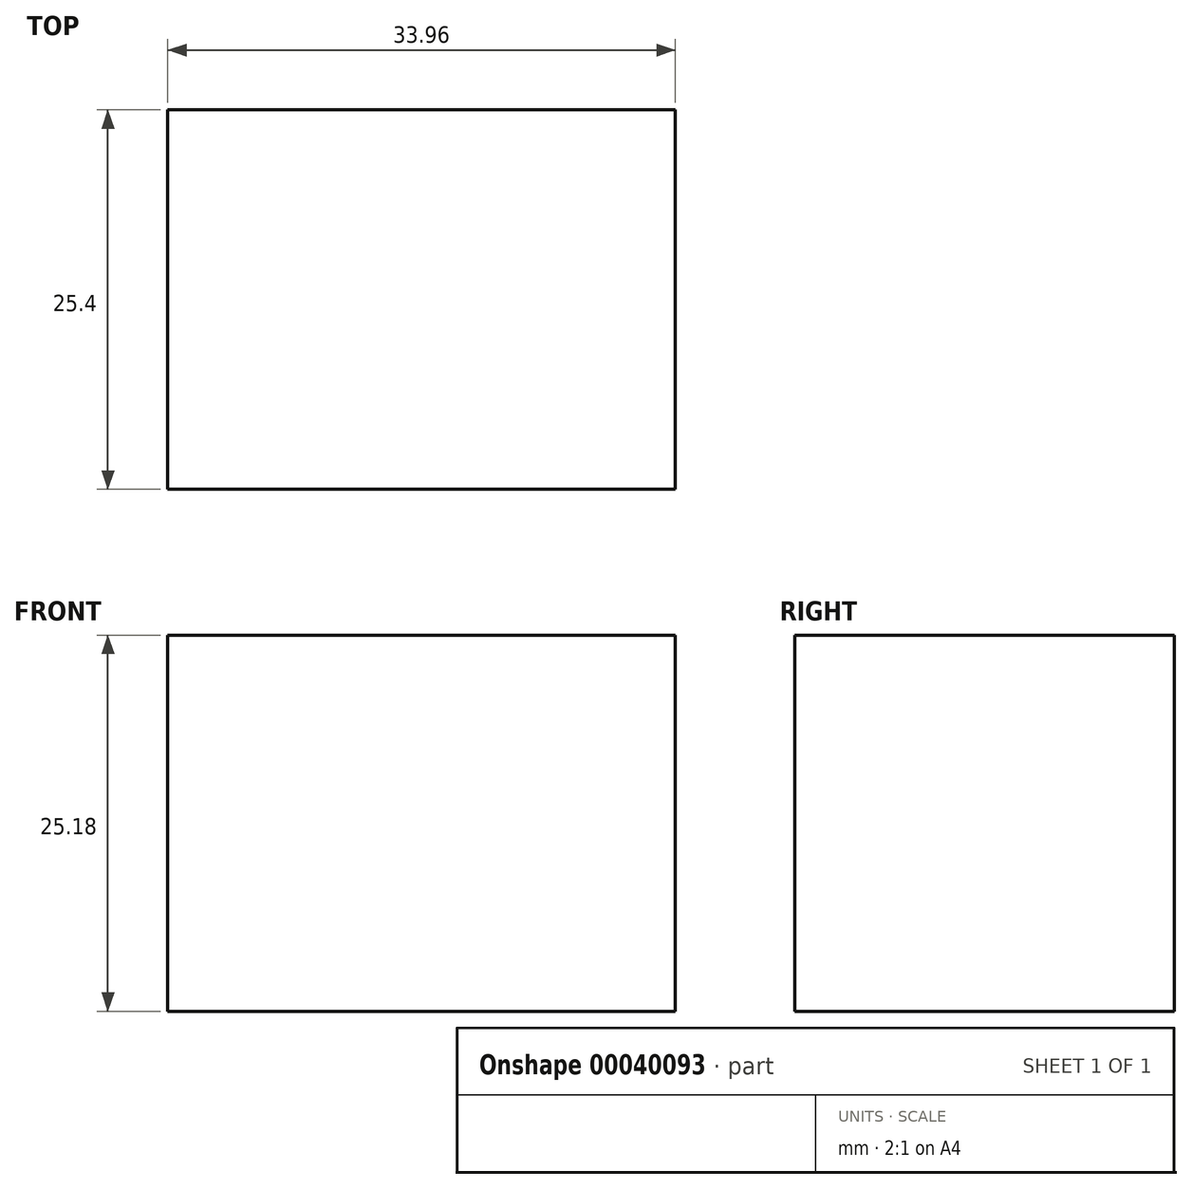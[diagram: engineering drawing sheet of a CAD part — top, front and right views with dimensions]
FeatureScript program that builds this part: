
annotation { "Feature Type Name" : "Feature", "Feature Type Description" : "" }
export const myFeature = defineFeature(function(context is Context, id is Id, definition is map)
    precondition{}
    {
        {
            var Q0;
            Q0=qCreatedBy(makeId("Front.planeOp"),FACE);
            var sketch = newSketch(context, id + "F0", { "sketchPlane" : qUnion([Q0])});
            skLineSegment(sketch, "E0.bottom", {"start": v(-16.79, 20.03) * mm, "end": v(17.17, 20.03) * mm});
            skLineSegment(sketch, "E0.top", {"start": v(-16.79, -5.15) * mm, "end": v(17.17, -5.15) * mm});
            skLineSegment(sketch, "E0.left", {"start": v(-16.79, 20.03) * mm, "end": v(-16.79, -5.15) * mm});
            skLineSegment(sketch, "E0.right", {"start": v(17.17, 20.03) * mm, "end": v(17.17, -5.15) * mm});
            skSolve(sketch);
        }
        {
            var Q0;
            Q0=makeQuery(id+"F0.imprint","IMPRINT",FACE,{"disambiguationData":[TD([[makeQuery(id+"F0.imprint","IMPRINT",EDGE,{"derivedFrom":sQuery(id+"F0.wireOp",EDGE,"E0.bottom")}),-1.0]])]});
            extrude(context, id + "F1", {"entities" : qUnion([Q0]), "depth" : 25.4 * mm});
        }
    });
